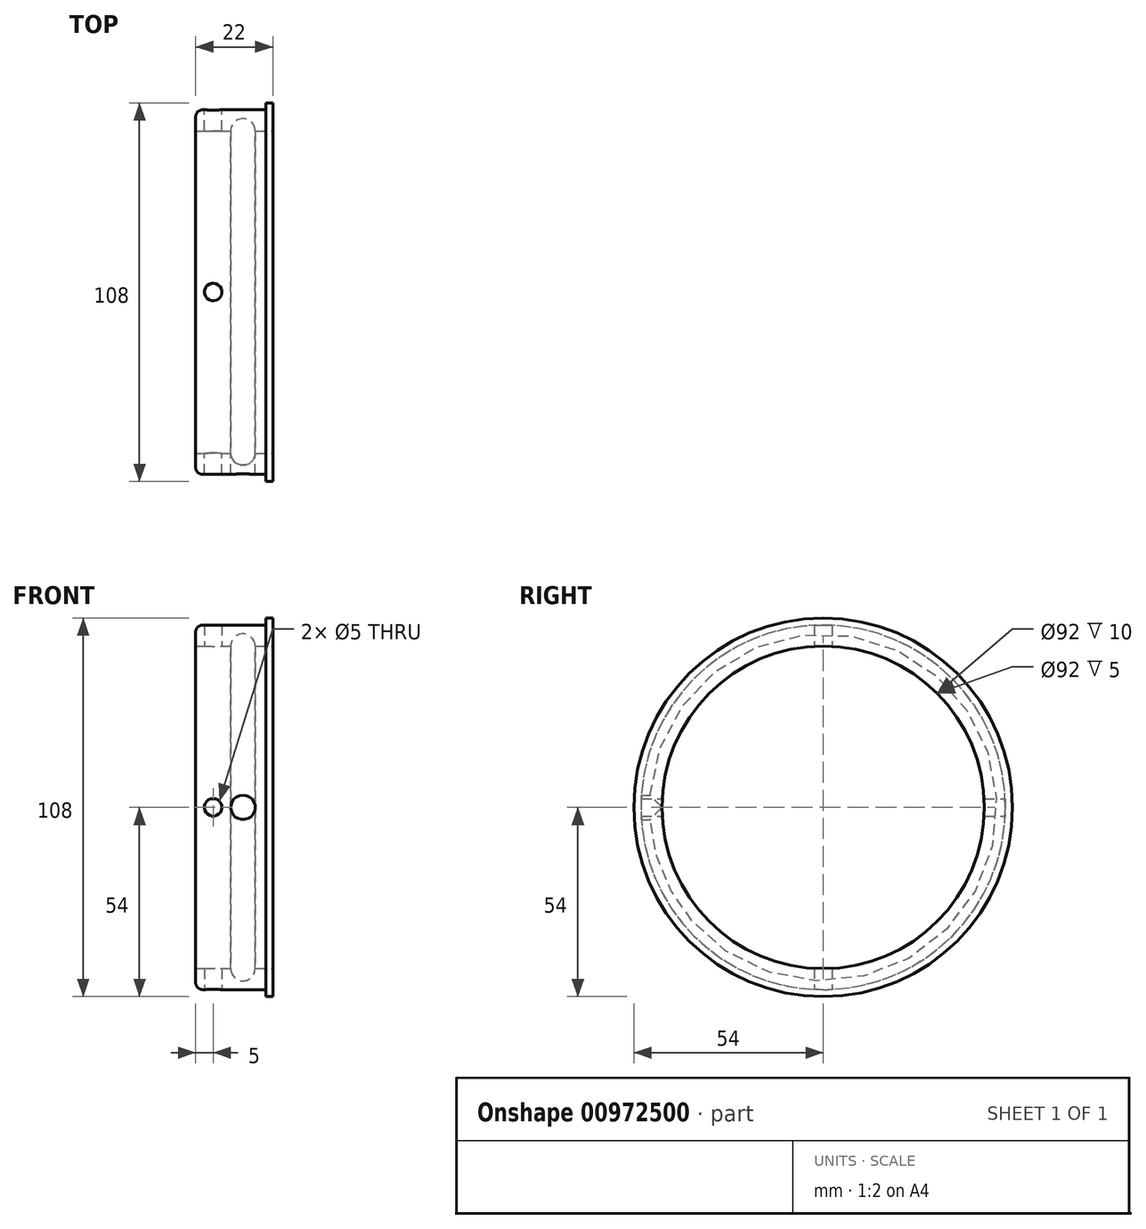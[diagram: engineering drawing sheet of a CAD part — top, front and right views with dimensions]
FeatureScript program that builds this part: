
annotation { "Feature Type Name" : "Feature", "Feature Type Description" : "" }
export const myFeature = defineFeature(function(context is Context, id is Id, definition is map)
    precondition{}
    {
        {
            var Q0;
            Q0=qCreatedBy(makeId("Front.planeOp"),FACE);
            var sketch = newSketch(context, id + "F0", { "sketchPlane" : qUnion([Q0])});
            skLineSegment(sketch, "E0", {"start": v(0, 0) * mm, "end": v(-98.35, 0) * mm, "construction": true});
            skLineSegment(sketch, "E1", {"start": v(0, 54) * mm, "end": v(-2, 54) * mm});
            skLineSegment(sketch, "E2", {"start": v(-2, 54) * mm, "end": v(-2, 52) * mm});
            skLineSegment(sketch, "E3", {"start": v(-2, 52) * mm, "end": v(-22, 52) * mm});
            skLineSegment(sketch, "E4", {"start": v(-22, 52) * mm, "end": v(-22, 46) * mm});
            skLineSegment(sketch, "E5", {"start": v(-22, 46) * mm, "end": v(0, 46) * mm});
            skLineSegment(sketch, "E6", {"start": v(0, 46) * mm, "end": v(0, 54) * mm});
            skArc(sketch, "E7", {"start": v(-5, 46) * mm, "mid": v(-8.5, 49.5) * mm, "end": v(-12, 46) * mm});
            skSolve(sketch);
        }
        {
            var Q0;
            Q0=makeQuery(id+"F0.imprint","IMPRINT",FACE,{"disambiguationData":[TD([[makeQuery(id+"F0.imprint","IMPRINT",EDGE,{"derivedFrom":sQuery(id+"F0.wireOp",EDGE,"E1")}),1.0]])]});
            var Q1;
            Q1=sQuery(id+"F0.wireOp",EDGE,"E0");
            revolve(context, id + "F1", {"surfaceOperationType" : NewSurfaceOperationType.NEW, "entities" : qUnion([Q0]), "axis" : qUnion([Q1]), "revolveType" : RevolveType.FULL});
        }
        {
            var Q0;
            Q0=makeQuery(id+"F1.opRevolve","SWEPT_EDGE",EDGE,{"disambiguationData":[OSD([sQuery(id+"F0.wireOp",EDGE,"E3"),sQuery(id+"F0.wireOp",EDGE,"E4")])]});
            fillet(context, id + "F2", {"entities" : qUnion([Q0]), "radius" : 2 * mm, "tangentPropagation" : true, "allowEdgeOverflow" : false});
        }
        {
            var Q0;
            Q0=qCreatedBy(makeId("Front.planeOp"),FACE);
            var sketch = newSketch(context, id + "F3", { "sketchPlane" : qUnion([Q0])});
            skCircle(sketch, "E8", {"center": v(-8.5, 0) * mm, "radius": 3.5 * mm});
            skSolve(sketch);
        }
        {
            var Q0;
            Q0 = qSketchRegion(id + "F3", true);
            var Q1;
            Q1 = qSketchRegion(id + "FTuSv3Nn5TyBptl_1", true);
            extrude(context, id + "F4", {"entities" : qUnion([Q0, Q1]), "operationType" : NewBodyOperationType.REMOVE, "depth" : 68.6 * mm, "offsetDistance" : 25 * mm});
        }
        {
            var Q0;
            Q0=qCreatedBy(makeId("Top.planeOp"),FACE);
            var sketch = newSketch(context, id + "F5", { "sketchPlane" : qUnion([Q0])});
            skCircle(sketch, "E9", {"center": v(-17, 0) * mm, "radius": 2.5 * mm});
            skSolve(sketch);
        }
        {
            var Q0;
            Q0 = qSketchRegion(id + "F5", true);
            extrude(context, id + "F6", {"entities" : qUnion([Q0]), "operationType" : NewBodyOperationType.REMOVE, "depth" : 70.9 * mm, "offsetDistance" : 25 * mm, "hasSecondDirection" : true, "secondDirectionOppositeDirection" : true, "secondDirectionDepth" : 64.5 * mm});
        }
        {
            var Q0;
            Q0=qCreatedBy(makeId("Front.planeOp"),FACE);
            var sketch = newSketch(context, id + "F7", { "sketchPlane" : qUnion([Q0])});
            skCircle(sketch, "E10", {"center": v(-17, 0) * mm, "radius": 2.5 * mm});
            skSolve(sketch);
        }
        {
            var Q0;
            Q0 = qSketchRegion(id + "F7", true);
            extrude(context, id + "F8", {"entities" : qUnion([Q0]), "operationType" : NewBodyOperationType.REMOVE, "depth" : 58.7 * mm, "offsetDistance" : 25 * mm, "hasSecondDirection" : true, "secondDirectionOppositeDirection" : true, "secondDirectionDepth" : 65.9 * mm});
        }
    });
